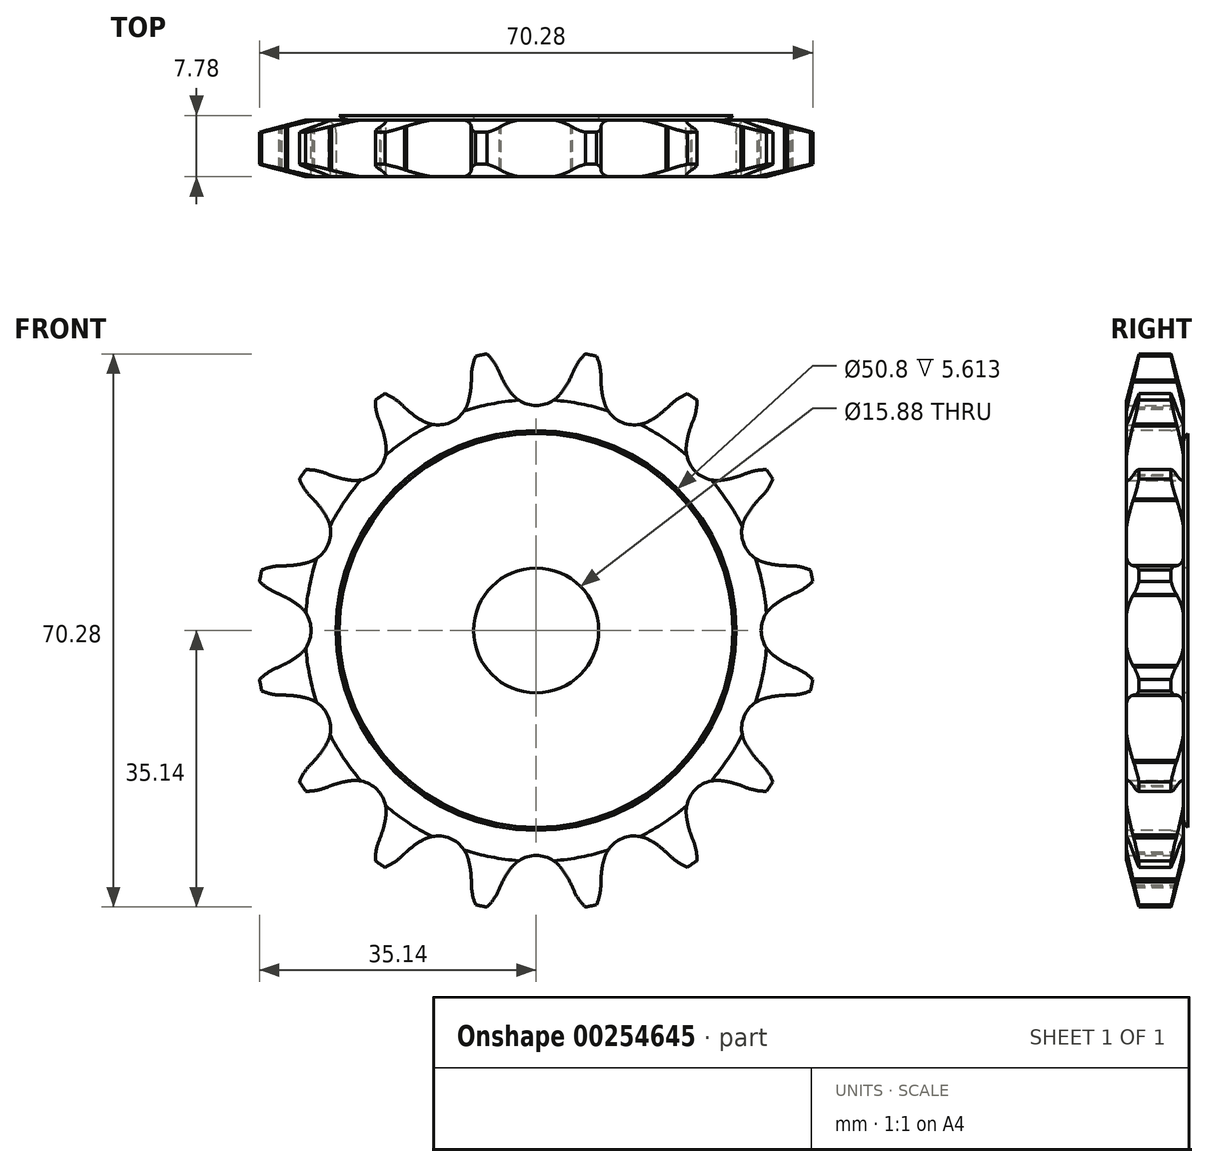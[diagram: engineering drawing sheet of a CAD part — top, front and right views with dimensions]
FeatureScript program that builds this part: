
annotation { "Feature Type Name" : "Feature", "Feature Type Description" : "" }
export const myFeature = defineFeature(function(context is Context, id is Id, definition is map)
    precondition{}
    {
        {
            var Q0;
            Q0=qCreatedBy(makeId("Right.planeOp"),FACE);
            var sketch = newSketch(context, id + "F0", { "sketchPlane" : qUnion([Q0])});
            skLineSegment(sketch, "E0", {"start": v(-7.78, 0) * mm, "end": v(14.45, 0) * mm});
            skLineSegment(sketch, "E1.bottom", {"start": v(-7.78, 7.94) * mm, "end": v(-0.56, 7.94) * mm});
            skLineSegment(sketch, "E1.top", {"start": v(-7.78, 35.69) * mm, "end": v(-0.56, 35.69) * mm});
            skLineSegment(sketch, "E1.left", {"start": v(-7.78, 7.94) * mm, "end": v(-7.78, 35.69) * mm});
            skLineSegment(sketch, "E1.right", {"start": v(-0.56, 7.94) * mm, "end": v(-0.56, 35.69) * mm});
            skLineSegment(sketch, "E2.bottom", {"start": v(-7.78, 7.94) * mm, "end": v(14.45, 7.94) * mm});
            skLineSegment(sketch, "E2.top", {"start": v(-7.78, 25.4) * mm, "end": v(14.45, 25.4) * mm});
            skLineSegment(sketch, "E2.left", {"start": v(-7.78, 7.94) * mm, "end": v(-7.78, 25.4) * mm});
            skLineSegment(sketch, "E2.right", {"start": v(14.45, 7.94) * mm, "end": v(14.45, 25.4) * mm});
            skLineSegment(sketch, "E3.MirrorCS", {"start": v(-7.78, -7.94) * mm, "end": v(-0.56, -7.94) * mm});
            skLineSegment(sketch, "E4.MirrorCS", {"start": v(-7.78, -25.4) * mm, "end": v(14.45, -25.4) * mm});
            skLineSegment(sketch, "E5.MirrorCS", {"start": v(-7.78, -35.69) * mm, "end": v(-0.56, -35.69) * mm});
            skLineSegment(sketch, "E6.MirrorCS", {"start": v(-7.78, -7.94) * mm, "end": v(-7.78, -35.69) * mm});
            skLineSegment(sketch, "E7.MirrorCS", {"start": v(-7.78, -7.94) * mm, "end": v(-7.78, -25.4) * mm});
            skLineSegment(sketch, "E8.MirrorCS", {"start": v(-7.78, -7.94) * mm, "end": v(14.45, -7.94) * mm});
            skLineSegment(sketch, "E9.MirrorCS", {"start": v(14.45, -7.94) * mm, "end": v(14.45, -25.4) * mm});
            skLineSegment(sketch, "E10.MirrorCS", {"start": v(-0.56, -7.94) * mm, "end": v(-0.56, -35.69) * mm});
            skSolve(sketch);
        }
        {
            var Q0;
            Q0=qCreatedBy(makeId("Front.planeOp"),FACE);
            var sketch = newSketch(context, id + "F1", { "sketchPlane" : qUnion([Q0])});
            skCircle(sketch, "E11", {"center": v(0, 0) * mm, "radius": 32.55 * mm, "construction": true});
            skLineSegment(sketch, "E12", {"start": v(0, 0) * mm, "end": v(0, 32.55) * mm, "construction": true});
            skLineSegment(sketch, "E13", {"start": v(0, 32.55) * mm, "end": v(77.8, 32.55) * mm, "construction": true});
            skLineSegment(sketch, "E14", {"start": v(0, 32.55) * mm, "end": v(5, 36.56) * mm, "construction": true});
            skLineSegment(sketch, "E15", {"start": v(5, 36.56) * mm, "end": v(-4.46, 32.3) * mm, "construction": true});
            skLineSegment(sketch, "E16", {"start": v(3.68, 14.24) * mm, "end": v(-4.46, 32.3) * mm});
            skLineSegment(sketch, "E17", {"start": v(0, 0) * mm, "end": v(-7.13, 35.85) * mm, "construction": true});
            skArc(sketch, "E18", {"start": v(-7.13, 35.85) * mm, "mid": v(-16.59, 27.19) * mm, "end": v(-4.24, 30.65) * mm, "construction": true});
            skLineSegment(sketch, "E19", {"start": v(-4.25, 30.83) * mm, "end": v(-4.25, 30.83) * mm});
            skArc(sketch, "E20", {"start": v(-4.46, 32.3) * mm, "mid": v(-3.84, 31.14) * mm, "end": v(-3.1, 30.07) * mm});
            skArc(sketch, "E21", {"start": v(-3.1, 30.07) * mm, "mid": v(13.83, 41.97) * mm, "end": v(-4.46, 32.3) * mm, "construction": true});
            skArc(sketch, "E22", {"start": v(-4.25, 30.83) * mm, "mid": v(-4.31, 31.4) * mm, "end": v(-4.43, 31.98) * mm});
            skArc(sketch, "E23", {"start": v(-4.24, 30.65) * mm, "mid": v(-4.24, 30.68) * mm, "end": v(-4.24, 30.7) * mm});
            skArc(sketch, "E24", {"start": v(-3.1, 30.07) * mm, "mid": v(1.22, 28.78) * mm, "end": v(3.96, 32.36) * mm});
            skArc(sketch, "E25", {"start": v(3.96, 32.36) * mm, "mid": v(-1.22, 36.32) * mm, "end": v(-3.1, 30.07) * mm, "construction": true});
            skLineSegment(sketch, "E26", {"start": v(-4.24, 30.7) * mm, "end": v(-4.24, 30.7) * mm});
            skArc(sketch, "E27", {"start": v(-4.24, 30.7) * mm, "mid": v(-4.25, 30.77) * mm, "end": v(-4.25, 30.83) * mm});
            skLineSegment(sketch, "E28", {"start": v(3.68, 14.24) * mm, "end": v(-12.66, 50.5) * mm});
            skLineSegment(sketch, "E29", {"start": v(3.4, 14.87) * mm, "end": v(0.55, 21.2) * mm});
            skLineSegment(sketch, "E30", {"start": v(3.4, 14.87) * mm, "end": v(-12.66, 50.5) * mm});
            skArc(sketch, "E31.MirrorCS", {"start": v(4.46, 32.3) * mm, "mid": v(3.84, 31.14) * mm, "end": v(3.1, 30.07) * mm});
            skLineSegment(sketch, "E32.MirrorCS", {"start": v(-3.4, 14.87) * mm, "end": v(12.66, 50.5) * mm});
            skArc(sketch, "E33.MirrorCS", {"start": v(4.24, 30.7) * mm, "mid": v(4.25, 30.77) * mm, "end": v(4.25, 30.83) * mm});
            skLineSegment(sketch, "E34.MirrorCS", {"start": v(4.25, 30.83) * mm, "end": v(4.25, 30.83) * mm});
            skLineSegment(sketch, "E35", {"start": v(4.46, 32.3) * mm, "end": v(12.66, 50.5) * mm});
            skLineSegment(sketch, "E36", {"start": v(3.4, 14.87) * mm, "end": v(3.68, 14.24) * mm});
            skArc(sketch, "E37", {"start": v(4.63, 32.63) * mm, "mid": v(5.62, 34.44) * mm, "end": v(7.13, 35.85) * mm});
            skArc(sketch, "E38", {"start": v(4.25, 30.83) * mm, "mid": v(4.38, 31.75) * mm, "end": v(4.63, 32.63) * mm});
            skLineSegment(sketch, "E39", {"start": v(4.46, 32.3) * mm, "end": v(4.63, 32.63) * mm});
            skLineSegment(sketch, "E40", {"start": v(-4.46, 32.3) * mm, "end": v(-4.59, 32.52) * mm});
            skArc(sketch, "E41", {"start": v(-4.59, 32.52) * mm, "mid": v(-5.59, 34.4) * mm, "end": v(-7.13, 35.85) * mm});
            skArc(sketch, "E42", {"start": v(-4.43, 31.98) * mm, "mid": v(-4.5, 32.25) * mm, "end": v(-4.59, 32.52) * mm});
            skLineSegment(sketch, "E43", {"start": v(-4.43, 31.98) * mm, "end": v(-4.43, 31.98) * mm});
            skArc(sketch, "E44.1.0", {"start": v(-16.69, 28.3) * mm, "mid": v(-18.33, 29.64) * mm, "end": v(-20.3, 30.4) * mm});
            skLineSegment(sketch, "E44.1.1", {"start": v(-16.48, 28.14) * mm, "end": v(-16.69, 28.3) * mm});
            skArc(sketch, "E44.1.2", {"start": v(-16.48, 28.14) * mm, "mid": v(-15.47, 27.3) * mm, "end": v(-14.36, 26.6) * mm});
            skArc(sketch, "E44.1.3", {"start": v(-14.36, 26.6) * mm, "mid": v(-9.88, 27.06) * mm, "end": v(-8.73, 31.41) * mm});
            skArc(sketch, "E44.1.4", {"start": v(-8.24, 31.55) * mm, "mid": v(-8.37, 30.24) * mm, "end": v(-8.65, 28.96) * mm});
            skLineSegment(sketch, "E44.1.5", {"start": v(-8.24, 31.55) * mm, "end": v(-8.21, 31.92) * mm});
            skArc(sketch, "E44.1.6", {"start": v(-8.21, 31.92) * mm, "mid": v(-7.98, 33.97) * mm, "end": v(-7.13, 35.85) * mm});
            skArc(sketch, "E44.2.0", {"start": v(-26.24, 19.75) * mm, "mid": v(-28.27, 20.37) * mm, "end": v(-30.4, 20.3) * mm});
            skLineSegment(sketch, "E44.2.1", {"start": v(-26, 19.69) * mm, "end": v(-26.24, 19.75) * mm});
            skArc(sketch, "E44.2.2", {"start": v(-26, 19.69) * mm, "mid": v(-24.74, 19.3) * mm, "end": v(-23.45, 19.08) * mm});
            skArc(sketch, "E44.2.3", {"start": v(-23.45, 19.08) * mm, "mid": v(-19.49, 21.22) * mm, "end": v(-20.08, 25.68) * mm});
            skArc(sketch, "E44.2.4", {"start": v(-19.69, 26) * mm, "mid": v(-19.3, 24.74) * mm, "end": v(-19.08, 23.45) * mm});
            skLineSegment(sketch, "E44.2.5", {"start": v(-19.69, 26) * mm, "end": v(-19.8, 26.34) * mm});
            skArc(sketch, "E44.2.6", {"start": v(-19.8, 26.34) * mm, "mid": v(-20.38, 28.33) * mm, "end": v(-20.3, 30.4) * mm});
            skArc(sketch, "E44.3.0", {"start": v(-31.8, 8.2) * mm, "mid": v(-33.91, 8) * mm, "end": v(-35.85, 7.13) * mm});
            skLineSegment(sketch, "E44.3.1", {"start": v(-31.55, 8.24) * mm, "end": v(-31.8, 8.2) * mm});
            skArc(sketch, "E44.3.2", {"start": v(-31.55, 8.24) * mm, "mid": v(-30.24, 8.37) * mm, "end": v(-28.96, 8.65) * mm});
            skArc(sketch, "E44.3.3", {"start": v(-28.96, 8.65) * mm, "mid": v(-26.12, 12.15) * mm, "end": v(-28.38, 16.04) * mm});
            skArc(sketch, "E44.3.4", {"start": v(-28.14, 16.48) * mm, "mid": v(-27.3, 15.47) * mm, "end": v(-26.6, 14.36) * mm});
            skLineSegment(sketch, "E44.3.5", {"start": v(-28.14, 16.48) * mm, "end": v(-28.38, 16.76) * mm});
            skArc(sketch, "E44.3.6", {"start": v(-28.38, 16.76) * mm, "mid": v(-29.66, 18.37) * mm, "end": v(-30.4, 20.3) * mm});
            skArc(sketch, "E44.4.0", {"start": v(-32.52, -4.59) * mm, "mid": v(-34.4, -5.59) * mm, "end": v(-35.85, -7.13) * mm});
            skLineSegment(sketch, "E44.4.1", {"start": v(-32.3, -4.46) * mm, "end": v(-32.52, -4.59) * mm});
            skArc(sketch, "E44.4.2", {"start": v(-32.3, -4.46) * mm, "mid": v(-31.14, -3.84) * mm, "end": v(-30.07, -3.1) * mm});
            skArc(sketch, "E44.4.3", {"start": v(-30.07, -3.1) * mm, "mid": v(-28.78, 1.22) * mm, "end": v(-32.36, 3.96) * mm});
            skArc(sketch, "E44.4.4", {"start": v(-32.3, 4.46) * mm, "mid": v(-31.14, 3.84) * mm, "end": v(-30.07, 3.1) * mm});
            skLineSegment(sketch, "E44.4.5", {"start": v(-32.3, 4.46) * mm, "end": v(-32.63, 4.63) * mm});
            skArc(sketch, "E44.4.6", {"start": v(-32.63, 4.63) * mm, "mid": v(-34.44, 5.62) * mm, "end": v(-35.85, 7.13) * mm});
            skArc(sketch, "E44.5.0", {"start": v(-28.3, -16.69) * mm, "mid": v(-29.64, -18.33) * mm, "end": v(-30.4, -20.3) * mm});
            skLineSegment(sketch, "E44.5.1", {"start": v(-28.14, -16.48) * mm, "end": v(-28.3, -16.69) * mm});
            skArc(sketch, "E44.5.2", {"start": v(-28.14, -16.48) * mm, "mid": v(-27.3, -15.47) * mm, "end": v(-26.6, -14.36) * mm});
            skArc(sketch, "E44.5.3", {"start": v(-26.6, -14.36) * mm, "mid": v(-27.06, -9.88) * mm, "end": v(-31.41, -8.73) * mm});
            skArc(sketch, "E44.5.4", {"start": v(-31.55, -8.24) * mm, "mid": v(-30.24, -8.37) * mm, "end": v(-28.96, -8.65) * mm});
            skLineSegment(sketch, "E44.5.5", {"start": v(-31.55, -8.24) * mm, "end": v(-31.92, -8.21) * mm});
            skArc(sketch, "E44.5.6", {"start": v(-31.92, -8.21) * mm, "mid": v(-33.97, -7.98) * mm, "end": v(-35.85, -7.13) * mm});
            skArc(sketch, "E44.6.0", {"start": v(-19.75, -26.24) * mm, "mid": v(-20.37, -28.27) * mm, "end": v(-20.3, -30.4) * mm});
            skLineSegment(sketch, "E44.6.1", {"start": v(-19.69, -26) * mm, "end": v(-19.75, -26.24) * mm});
            skArc(sketch, "E44.6.2", {"start": v(-19.69, -26) * mm, "mid": v(-19.3, -24.74) * mm, "end": v(-19.08, -23.45) * mm});
            skArc(sketch, "E44.6.3", {"start": v(-19.08, -23.45) * mm, "mid": v(-21.22, -19.49) * mm, "end": v(-25.68, -20.08) * mm});
            skArc(sketch, "E44.6.4", {"start": v(-26, -19.69) * mm, "mid": v(-24.74, -19.3) * mm, "end": v(-23.45, -19.08) * mm});
            skLineSegment(sketch, "E44.6.5", {"start": v(-26, -19.69) * mm, "end": v(-26.34, -19.8) * mm});
            skArc(sketch, "E44.6.6", {"start": v(-26.34, -19.8) * mm, "mid": v(-28.33, -20.38) * mm, "end": v(-30.4, -20.3) * mm});
            skArc(sketch, "E44.7.0", {"start": v(-8.2, -31.8) * mm, "mid": v(-8, -33.91) * mm, "end": v(-7.13, -35.85) * mm});
            skLineSegment(sketch, "E44.7.1", {"start": v(-8.24, -31.55) * mm, "end": v(-8.2, -31.8) * mm});
            skArc(sketch, "E44.7.2", {"start": v(-8.24, -31.55) * mm, "mid": v(-8.37, -30.24) * mm, "end": v(-8.65, -28.96) * mm});
            skArc(sketch, "E44.7.3", {"start": v(-8.65, -28.96) * mm, "mid": v(-12.15, -26.12) * mm, "end": v(-16.04, -28.38) * mm});
            skArc(sketch, "E44.7.4", {"start": v(-16.48, -28.14) * mm, "mid": v(-15.47, -27.3) * mm, "end": v(-14.36, -26.6) * mm});
            skLineSegment(sketch, "E44.7.5", {"start": v(-16.48, -28.14) * mm, "end": v(-16.76, -28.38) * mm});
            skArc(sketch, "E44.7.6", {"start": v(-16.76, -28.38) * mm, "mid": v(-18.37, -29.66) * mm, "end": v(-20.3, -30.4) * mm});
            skArc(sketch, "E44.8.0", {"start": v(4.59, -32.52) * mm, "mid": v(5.59, -34.4) * mm, "end": v(7.13, -35.85) * mm});
            skLineSegment(sketch, "E44.8.1", {"start": v(4.46, -32.3) * mm, "end": v(4.59, -32.52) * mm});
            skArc(sketch, "E44.8.2", {"start": v(4.46, -32.3) * mm, "mid": v(3.84, -31.14) * mm, "end": v(3.1, -30.07) * mm});
            skArc(sketch, "E44.8.3", {"start": v(3.1, -30.07) * mm, "mid": v(-1.22, -28.78) * mm, "end": v(-3.96, -32.36) * mm});
            skArc(sketch, "E44.8.4", {"start": v(-4.46, -32.3) * mm, "mid": v(-3.84, -31.14) * mm, "end": v(-3.1, -30.07) * mm});
            skLineSegment(sketch, "E44.8.5", {"start": v(-4.46, -32.3) * mm, "end": v(-4.63, -32.63) * mm});
            skArc(sketch, "E44.8.6", {"start": v(-4.63, -32.63) * mm, "mid": v(-5.62, -34.44) * mm, "end": v(-7.13, -35.85) * mm});
            skArc(sketch, "E44.9.0", {"start": v(16.69, -28.3) * mm, "mid": v(18.33, -29.64) * mm, "end": v(20.3, -30.4) * mm});
            skLineSegment(sketch, "E44.9.1", {"start": v(16.48, -28.14) * mm, "end": v(16.69, -28.3) * mm});
            skArc(sketch, "E44.9.2", {"start": v(16.48, -28.14) * mm, "mid": v(15.47, -27.3) * mm, "end": v(14.36, -26.6) * mm});
            skArc(sketch, "E44.9.3", {"start": v(14.36, -26.6) * mm, "mid": v(9.88, -27.06) * mm, "end": v(8.73, -31.41) * mm});
            skArc(sketch, "E44.9.4", {"start": v(8.24, -31.55) * mm, "mid": v(8.37, -30.24) * mm, "end": v(8.65, -28.96) * mm});
            skLineSegment(sketch, "E44.9.5", {"start": v(8.24, -31.55) * mm, "end": v(8.21, -31.92) * mm});
            skArc(sketch, "E44.9.6", {"start": v(8.21, -31.92) * mm, "mid": v(7.98, -33.97) * mm, "end": v(7.13, -35.85) * mm});
            skArc(sketch, "E44.10.0", {"start": v(26.24, -19.75) * mm, "mid": v(28.27, -20.37) * mm, "end": v(30.4, -20.3) * mm});
            skLineSegment(sketch, "E44.10.1", {"start": v(26, -19.69) * mm, "end": v(26.24, -19.75) * mm});
            skArc(sketch, "E44.10.2", {"start": v(26, -19.69) * mm, "mid": v(24.74, -19.3) * mm, "end": v(23.45, -19.08) * mm});
            skArc(sketch, "E44.10.3", {"start": v(23.45, -19.08) * mm, "mid": v(19.49, -21.22) * mm, "end": v(20.08, -25.68) * mm});
            skArc(sketch, "E44.10.4", {"start": v(19.69, -26) * mm, "mid": v(19.3, -24.74) * mm, "end": v(19.08, -23.45) * mm});
            skLineSegment(sketch, "E44.10.5", {"start": v(19.69, -26) * mm, "end": v(19.8, -26.34) * mm});
            skArc(sketch, "E44.10.6", {"start": v(19.8, -26.34) * mm, "mid": v(20.38, -28.33) * mm, "end": v(20.3, -30.4) * mm});
            skArc(sketch, "E44.11.0", {"start": v(31.8, -8.2) * mm, "mid": v(33.91, -8) * mm, "end": v(35.85, -7.13) * mm});
            skLineSegment(sketch, "E44.11.1", {"start": v(31.55, -8.24) * mm, "end": v(31.8, -8.2) * mm});
            skArc(sketch, "E44.11.2", {"start": v(31.55, -8.24) * mm, "mid": v(30.24, -8.37) * mm, "end": v(28.96, -8.65) * mm});
            skArc(sketch, "E44.11.3", {"start": v(28.96, -8.65) * mm, "mid": v(26.12, -12.15) * mm, "end": v(28.38, -16.04) * mm});
            skArc(sketch, "E44.11.4", {"start": v(28.14, -16.48) * mm, "mid": v(27.3, -15.47) * mm, "end": v(26.6, -14.36) * mm});
            skLineSegment(sketch, "E44.11.5", {"start": v(28.14, -16.48) * mm, "end": v(28.38, -16.76) * mm});
            skArc(sketch, "E44.11.6", {"start": v(28.38, -16.76) * mm, "mid": v(29.66, -18.37) * mm, "end": v(30.4, -20.3) * mm});
            skArc(sketch, "E44.12.0", {"start": v(32.52, 4.59) * mm, "mid": v(34.4, 5.59) * mm, "end": v(35.85, 7.13) * mm});
            skLineSegment(sketch, "E44.12.1", {"start": v(32.3, 4.46) * mm, "end": v(32.52, 4.59) * mm});
            skArc(sketch, "E44.12.2", {"start": v(32.3, 4.46) * mm, "mid": v(31.14, 3.84) * mm, "end": v(30.07, 3.1) * mm});
            skArc(sketch, "E44.12.3", {"start": v(30.07, 3.1) * mm, "mid": v(28.78, -1.22) * mm, "end": v(32.36, -3.96) * mm});
            skArc(sketch, "E44.12.4", {"start": v(32.3, -4.46) * mm, "mid": v(31.14, -3.84) * mm, "end": v(30.07, -3.1) * mm});
            skLineSegment(sketch, "E44.12.5", {"start": v(32.3, -4.46) * mm, "end": v(32.63, -4.63) * mm});
            skArc(sketch, "E44.12.6", {"start": v(32.63, -4.63) * mm, "mid": v(34.44, -5.62) * mm, "end": v(35.85, -7.13) * mm});
            skArc(sketch, "E44.13.0", {"start": v(28.3, 16.69) * mm, "mid": v(29.64, 18.33) * mm, "end": v(30.4, 20.3) * mm});
            skLineSegment(sketch, "E44.13.1", {"start": v(28.14, 16.48) * mm, "end": v(28.3, 16.69) * mm});
            skArc(sketch, "E44.13.2", {"start": v(28.14, 16.48) * mm, "mid": v(27.3, 15.47) * mm, "end": v(26.6, 14.36) * mm});
            skArc(sketch, "E44.13.3", {"start": v(26.6, 14.36) * mm, "mid": v(27.06, 9.88) * mm, "end": v(31.41, 8.73) * mm});
            skArc(sketch, "E44.13.4", {"start": v(31.55, 8.24) * mm, "mid": v(30.24, 8.37) * mm, "end": v(28.96, 8.65) * mm});
            skLineSegment(sketch, "E44.13.5", {"start": v(31.55, 8.24) * mm, "end": v(31.92, 8.21) * mm});
            skArc(sketch, "E44.13.6", {"start": v(31.92, 8.21) * mm, "mid": v(33.97, 7.98) * mm, "end": v(35.85, 7.13) * mm});
            skArc(sketch, "E44.14.0", {"start": v(19.75, 26.24) * mm, "mid": v(20.37, 28.27) * mm, "end": v(20.3, 30.4) * mm});
            skLineSegment(sketch, "E44.14.1", {"start": v(19.69, 26) * mm, "end": v(19.75, 26.24) * mm});
            skArc(sketch, "E44.14.2", {"start": v(19.69, 26) * mm, "mid": v(19.3, 24.74) * mm, "end": v(19.08, 23.45) * mm});
            skArc(sketch, "E44.14.3", {"start": v(19.08, 23.45) * mm, "mid": v(21.22, 19.49) * mm, "end": v(25.68, 20.08) * mm});
            skArc(sketch, "E44.14.4", {"start": v(26, 19.69) * mm, "mid": v(24.74, 19.3) * mm, "end": v(23.45, 19.08) * mm});
            skLineSegment(sketch, "E44.14.5", {"start": v(26, 19.69) * mm, "end": v(26.34, 19.8) * mm});
            skArc(sketch, "E44.14.6", {"start": v(26.34, 19.8) * mm, "mid": v(28.33, 20.38) * mm, "end": v(30.4, 20.3) * mm});
            skArc(sketch, "E44.15.0", {"start": v(8.2, 31.8) * mm, "mid": v(8, 33.91) * mm, "end": v(7.13, 35.85) * mm});
            skLineSegment(sketch, "E44.15.1", {"start": v(8.24, 31.55) * mm, "end": v(8.2, 31.8) * mm});
            skArc(sketch, "E44.15.2", {"start": v(8.24, 31.55) * mm, "mid": v(8.37, 30.24) * mm, "end": v(8.65, 28.96) * mm});
            skArc(sketch, "E44.15.3", {"start": v(8.65, 28.96) * mm, "mid": v(12.15, 26.12) * mm, "end": v(16.04, 28.38) * mm});
            skArc(sketch, "E44.15.4", {"start": v(16.48, 28.14) * mm, "mid": v(15.47, 27.3) * mm, "end": v(14.36, 26.6) * mm});
            skLineSegment(sketch, "E44.15.5", {"start": v(16.48, 28.14) * mm, "end": v(16.76, 28.38) * mm});
            skArc(sketch, "E44.15.6", {"start": v(16.76, 28.38) * mm, "mid": v(18.37, 29.66) * mm, "end": v(20.3, 30.4) * mm});
            skSolve(sketch);
        }
        {
            var Q0;
            {var subQ5=sQuery(id+"F0.wireOp",EDGE,"E2.right");Q0=makeQuery(id+"F0.imprint","IMPRINT",FACE,{"disambiguationData":[TD([[makeQuery(id+"F0.imprint","IMPRINT",EDGE,{"derivedFrom":subQ5}),1.0]])]});}
            var Q1;
            {var subQ5=sQuery(id+"F0.wireOp",EDGE,"E2.left");Q1=makeQuery(id+"F0.imprint","IMPRINT",FACE,{"disambiguationData":[TD([[makeQuery(id+"F0.imprint","IMPRINT",EDGE,{"derivedFrom":subQ5}),-1.0]])]});}
            var Q2;
            {var subQ0=sQuery(id+"F0.wireOp",EDGE,"E1.top");Q2=makeQuery(id+"F0.imprint","IMPRINT",FACE,{"disambiguationData":[TD([[makeQuery(id+"F0.imprint","IMPRINT",EDGE,{"derivedFrom":subQ0}),-1.0]])]});}
            var Q3;
            Q3=sQuery(id+"F0.wireOp",EDGE,"E0");
            revolve(context, id + "F2", {"entities" : qUnion([Q0, Q1, Q2]), "axis" : qUnion([Q3]), "revolveType" : RevolveType.FULL});
        }
        {
            var Q0;
            Q0=makeQuery(id+"F2.opRevolve","SWEPT_EDGE",EDGE,{"disambiguationData":[OSD([sQuery(id+"F0.wireOp",EDGE,"E1.right"),sQuery(id+"F0.wireOp",EDGE,"E2.top")])]});
            fillet(context, id + "F3", {"entities" : qUnion([Q0]), "radius" : 1.6 * mm, "tangentPropagation" : true, "allowEdgeOverflow" : false});
        }
        {
            var Q0;
            Q0=makeQuery(id+"F2.opRevolve","SWEPT_EDGE",EDGE,{"disambiguationData":[OSD([sQuery(id+"F0.wireOp",EDGE,"E2.top"),sQuery(id+"F0.wireOp",EDGE,"E2.right")])]});
            chamfer(context, id + "F4", {"entities" : qUnion([Q0]), "width" : 0.79 * mm, "tangentPropagation" : true});
        }
        {
            var Q0;
            Q0=makeQuery(id+"F2.opRevolve","SWEPT_EDGE",EDGE,{"disambiguationData":[OSD([sQuery(id+"F0.wireOp",EDGE,"E1.top"),sQuery(id+"F0.wireOp",EDGE,"E1.left")])]});
            var Q1;
            Q1=makeQuery(id+"F2.opRevolve","SWEPT_EDGE",EDGE,{"disambiguationData":[OSD([sQuery(id+"F0.wireOp",EDGE,"E1.top"),sQuery(id+"F0.wireOp",EDGE,"E1.right")])]});
            chamfer(context, id + "F5", {"entities" : qUnion([Q0, Q1]), "chamferType" : ChamferType.TWO_OFFSETS, "width1" : 6.35 * mm, "oppositeDirection" : false, "width2" : 1.57 * mm, "tangentPropagation" : true});
        }
        {
            var Q0;
            Q0 = qSketchRegion(id + "F1", true);
            extrude(context, id + "F6", {"entities" : qUnion([Q0]), "operationType" : NewBodyOperationType.INTERSECT, "endBound" : BoundingType.THROUGH_ALL, "depth" : 25.4 * mm});
        }
    });
